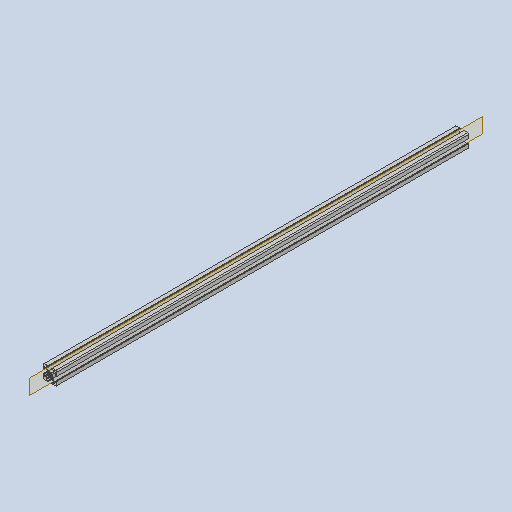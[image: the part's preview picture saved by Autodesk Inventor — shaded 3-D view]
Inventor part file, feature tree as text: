
AUTODESK INVENTOR PART (.ipt)
format: ipt  version: 2023 (Build 270158000, 158)  size: 391,168 bytes
history: native  units: mm
features: plane x2, extrude x1, sketch x1
ambient origin geometry x8: Origin, YZ Plane, XZ Plane, XY Plane, X Axis, Y Axis, Z Axis, Center Point
bodies: Solid1 (feature_tree)
feature tree (4):
  extrude  "Extrusion1"  [1 undecoded]
  plane  "Work Plane1"
  plane  "Work Plane2"
  sketch  "Sketch_1"  dims[d0=600.0mm d1=0.0mm]
note: 1 required parameter value undecoded (feature->parameter linkage not recoverable at this tier; creation-order binding heuristic only, values carry confidence <= 0.55)
